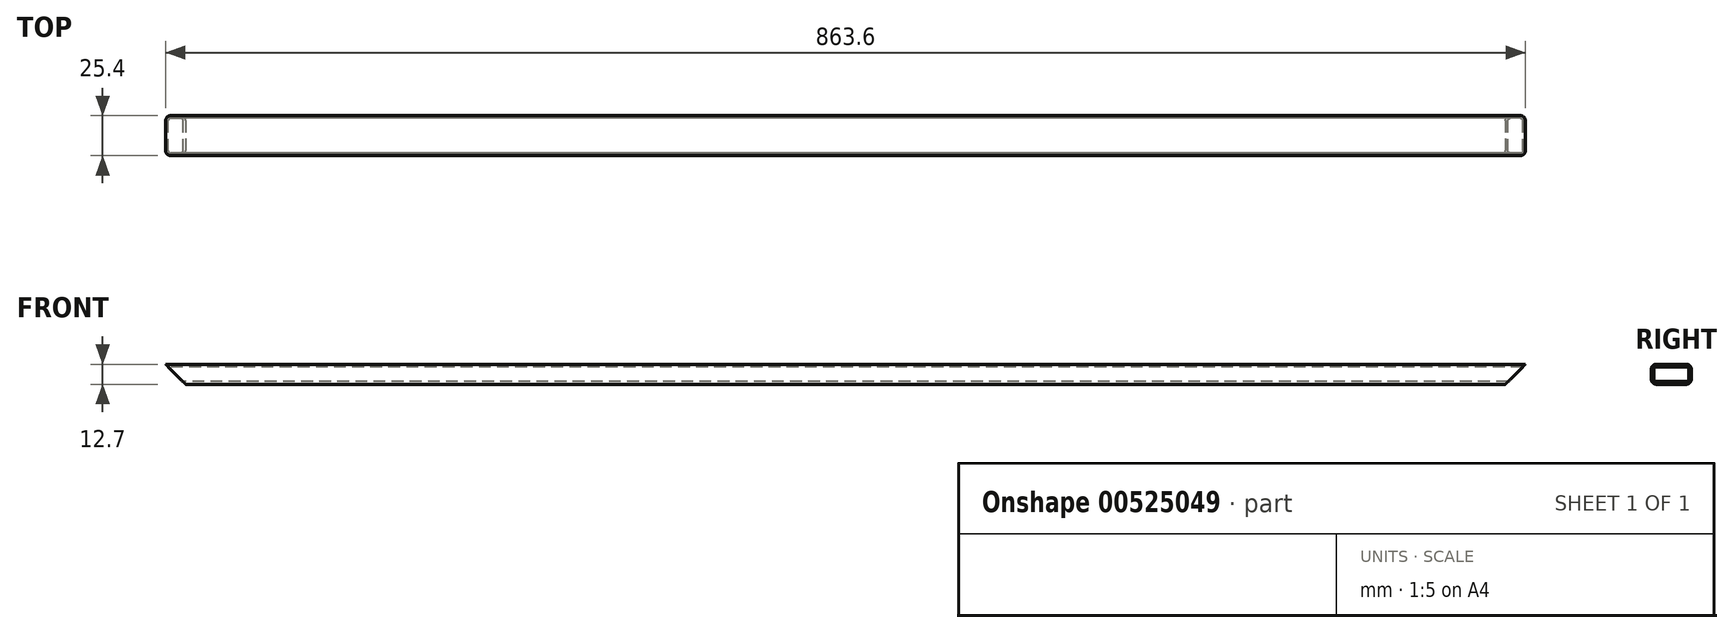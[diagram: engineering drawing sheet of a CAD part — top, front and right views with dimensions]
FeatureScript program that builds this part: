
annotation { "Feature Type Name" : "Feature", "Feature Type Description" : "" }
export const myFeature = defineFeature(function(context is Context, id is Id, definition is map)
    precondition{}
    {
        {
            var Q0;
            Q0=qCreatedBy(makeId("Right.planeOp"),FACE);
            var sketch = newSketch(context, id + "F0", { "sketchPlane" : qUnion([Q0])});
            skLineSegment(sketch, "E0.bottom", {"start": v(-9.53, 4.7) * mm, "end": v(9.53, 4.7) * mm});
            skLineSegment(sketch, "E0.top", {"start": v(-9.53, -4.7) * mm, "end": v(9.53, -4.7) * mm});
            skLineSegment(sketch, "E0.left", {"start": v(-11.05, 3.17) * mm, "end": v(-11.05, -3.18) * mm});
            skLineSegment(sketch, "E0.right", {"start": v(11.05, 3.18) * mm, "end": v(11.05, -3.18) * mm});
            skPoint(sketch, "E1.visualSharp", {"position": v(-11.05, 4.7) * mm});
            skArc(sketch, "E1.filletArc", {"start": v(-9.53, 4.7) * mm, "mid": v(-10.6, 4.25) * mm, "end": v(-11.05, 3.17) * mm});
            skPoint(sketch, "E2.visualSharp", {"position": v(-11.05, -4.7) * mm});
            skArc(sketch, "E2.filletArc", {"start": v(-11.05, -3.18) * mm, "mid": v(-10.6, -4.25) * mm, "end": v(-9.53, -4.7) * mm});
            skPoint(sketch, "E3.visualSharp", {"position": v(11.05, -4.7) * mm});
            skArc(sketch, "E3.filletArc", {"start": v(9.53, -4.7) * mm, "mid": v(10.6, -4.25) * mm, "end": v(11.05, -3.18) * mm});
            skPoint(sketch, "E4.visualSharp", {"position": v(11.05, 4.7) * mm});
            skArc(sketch, "E4.filletArc", {"start": v(11.05, 3.18) * mm, "mid": v(10.6, 4.25) * mm, "end": v(9.53, 4.7) * mm});
            skArc(sketch, "E5.0", {"start": v(-12.7, -3.18) * mm, "mid": v(-11.77, -5.42) * mm, "end": v(-9.53, -6.35) * mm});
            skLineSegment(sketch, "E5.1", {"start": v(-12.7, 3.18) * mm, "end": v(-12.7, -3.18) * mm});
            skLineSegment(sketch, "E5.2", {"start": v(-9.53, -6.35) * mm, "end": v(9.53, -6.35) * mm});
            skArc(sketch, "E5.3", {"start": v(-9.53, 6.35) * mm, "mid": v(-11.77, 5.42) * mm, "end": v(-12.7, 3.18) * mm});
            skArc(sketch, "E5.4", {"start": v(9.53, -6.35) * mm, "mid": v(11.77, -5.42) * mm, "end": v(12.7, -3.17) * mm});
            skLineSegment(sketch, "E5.5", {"start": v(12.7, 3.18) * mm, "end": v(12.7, -3.18) * mm});
            skArc(sketch, "E5.6", {"start": v(12.7, 3.17) * mm, "mid": v(11.77, 5.42) * mm, "end": v(9.53, 6.35) * mm});
            skLineSegment(sketch, "E5.7", {"start": v(-9.53, 6.35) * mm, "end": v(9.53, 6.35) * mm});
            skPoint(sketch, "E6", {"position": v(0, 4.7) * mm});
            skPoint(sketch, "E7", {"position": v(11.05, 0) * mm});
            skSolve(sketch);
        }
        {
            var Q0;
            Q0=qSketchRegion(id+"F0",true);
            extrude(context, id + "F1", {"entities" : qUnion([Q0]), "endBound" : BoundingType.SYMMETRIC, "depth" : 863.6 * mm, "offsetDistance" : 25.4 * mm});
        }
        {
            var Q0;
            Q0=qCreatedBy(makeId("Front.planeOp"),FACE);
            var sketch = newSketch(context, id + "F2", { "sketchPlane" : qUnion([Q0])});
            skLineSegment(sketch, "E8", {"start": v(-431.8, -6.35) * mm, "end": v(-419.1, -6.35) * mm});
            skLineSegment(sketch, "E9", {"start": v(-419.1, -6.35) * mm, "end": v(-431.8, 6.35) * mm});
            skLineSegment(sketch, "E10", {"start": v(-431.8, 6.35) * mm, "end": v(-431.8, -6.35) * mm});
            skLineSegment(sketch, "E11", {"start": v(0, 0) * mm, "end": v(0, 18.5) * mm, "construction": true});
            skLineSegment(sketch, "E12.MirrorCS", {"start": v(431.8, -6.35) * mm, "end": v(419.1, -6.35) * mm});
            skLineSegment(sketch, "E13.MirrorCS", {"start": v(419.1, -6.35) * mm, "end": v(431.8, 6.35) * mm});
            skLineSegment(sketch, "E14.MirrorCS", {"start": v(431.8, 6.35) * mm, "end": v(431.8, -6.35) * mm});
            skSolve(sketch);
        }
        {
            var Q0;
            Q0=qSketchRegion(id+"F2",true);
            extrude(context, id + "F3", {"entities" : qUnion([Q0]), "operationType" : NewBodyOperationType.REMOVE, "endBound" : BoundingType.THROUGH_ALL, "oppositeDirection" : true, "depth" : 25.4 * mm, "offsetDistance" : 25.4 * mm, "hasSecondDirection" : true, "secondDirectionBound" : SecondDirectionBoundingType.THROUGH_ALL, "secondDirectionOppositeDirection" : false, "secondDirectionDepth" : 25.4 * mm});
        }
    });
